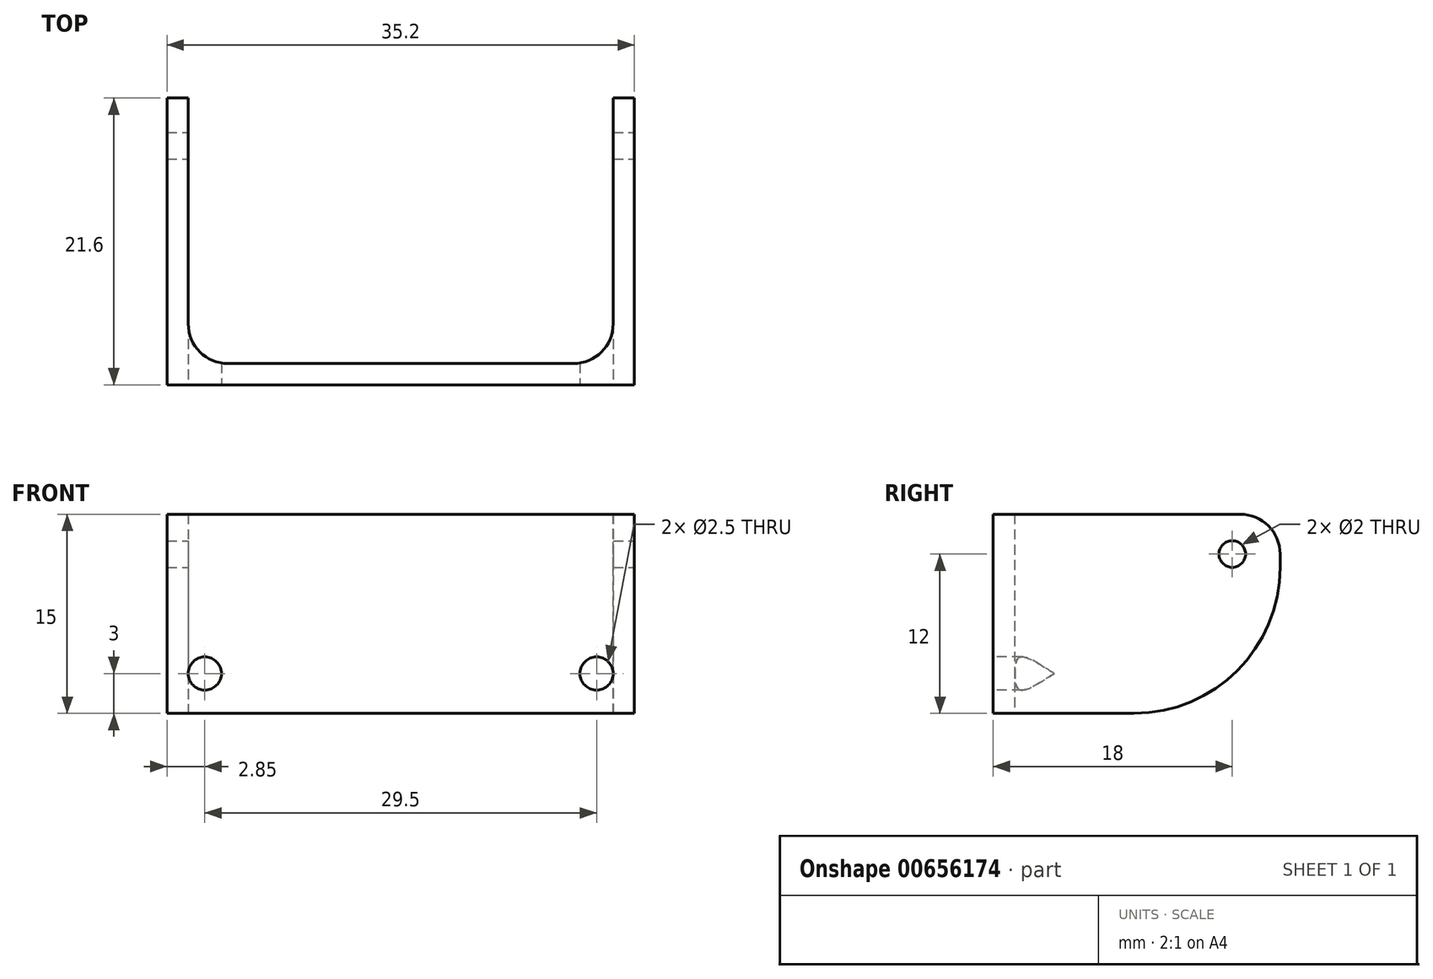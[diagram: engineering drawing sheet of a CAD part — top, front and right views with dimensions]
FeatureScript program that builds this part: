
annotation { "Feature Type Name" : "Feature", "Feature Type Description" : "" }
export const myFeature = defineFeature(function(context is Context, id is Id, definition is map)
    precondition{}
    {
        {
            var Q0;
            Q0=qCreatedBy(makeId("Top.planeOp"),FACE);
            var sketch = newSketch(context, id + "F0", { "sketchPlane" : qUnion([Q0])});
            skLineSegment(sketch, "E0", {"start": v(0, 0) * mm, "end": v(0, -21.6) * mm});
            skLineSegment(sketch, "E1", {"start": v(0, -21.6) * mm, "end": v(35.2, -21.6) * mm});
            skLineSegment(sketch, "E2", {"start": v(35.2, -21.6) * mm, "end": v(35.2, 0) * mm});
            skLineSegment(sketch, "E3", {"start": v(35.2, 0) * mm, "end": v(33.6, 0) * mm});
            skLineSegment(sketch, "E4", {"start": v(33.6, 0) * mm, "end": v(33.6, -17) * mm});
            skLineSegment(sketch, "E5", {"start": v(30.6, -20) * mm, "end": v(4.6, -20) * mm});
            skLineSegment(sketch, "E6", {"start": v(1.6, -17) * mm, "end": v(1.6, 0) * mm});
            skLineSegment(sketch, "E7", {"start": v(1.6, 0) * mm, "end": v(0, 0) * mm});
            skPoint(sketch, "E8.visualSharp", {"position": v(1.6, -20) * mm});
            skArc(sketch, "E8.filletArc", {"start": v(1.6, -17) * mm, "mid": v(2.48, -19.12) * mm, "end": v(4.6, -20) * mm});
            skPoint(sketch, "E9.visualSharp", {"position": v(33.6, -20) * mm});
            skArc(sketch, "E9.filletArc", {"start": v(30.6, -20) * mm, "mid": v(32.72, -19.12) * mm, "end": v(33.6, -17) * mm});
            skSolve(sketch);
        }
        {
            var Q0;
            Q0=makeQuery(id+"F0.imprint","IMPRINT",FACE,{"disambiguationData":[TD([[makeQuery(id+"F0.imprint","IMPRINT",EDGE,{"derivedFrom":sQuery(id+"F0.wireOp",EDGE,"E0")}),1.0]])]});
            extrude(context, id + "F1", {"entities" : qUnion([Q0]), "depth" : 15 * mm});
        }
        {
            var Q0;
            Q0=makeQuery(id+"F1.opExtrude","SWEPT_FACE",FACE,{"disambiguationData":[OSD([sQuery(id+"F0.wireOp",EDGE,"E1")])]});
            var sketch = newSketch(context, id + "F2", { "sketchPlane" : qUnion([Q0])});
            skLineSegment(sketch, "E10", {"start": v(2.85, 3) * mm, "end": v(32.35, 3) * mm, "construction": true});
            skLineSegment(sketch, "E11", {"start": v(17.6, 0) * mm, "end": v(17.6, 3) * mm, "construction": true});
            skCircle(sketch, "E12", {"center": v(2.85, 3) * mm, "radius": 1.25 * mm});
            skCircle(sketch, "E13", {"center": v(32.35, 3) * mm, "radius": 1.25 * mm});
            skSolve(sketch);
        }
        {
            var Q0;
            Q0=qSketchRegion(id+"F2",true);
            extrude(context, id + "F3", {"entities" : qUnion([Q0]), "operationType" : NewBodyOperationType.REMOVE, "oppositeDirection" : true, "depth" : 25 * mm});
        }
        {
            var Q0;
            Q0=makeQuery(id+"F1.opExtrude","SWEPT_FACE",FACE,{"disambiguationData":[OSD([sQuery(id+"F0.wireOp",EDGE,"E2")])]});
            var sketch = newSketch(context, id + "F4", { "sketchPlane" : qUnion([Q0])});
            skCircle(sketch, "E14", {"center": v(-3.6, 12) * mm, "radius": 1 * mm});
            skSolve(sketch);
        }
        {
            var Q0;
            Q0=makeQuery(id+"F4.imprint","IMPRINT",FACE,{"disambiguationData":[TD([[makeQuery(id+"F4.imprint","IMPRINT",EDGE,{"derivedFrom":sQuery(id+"F4.wireOp",EDGE,"E14")}),1.0]])]});
            extrude(context, id + "F5", {"entities" : qUnion([Q0]), "operationType" : NewBodyOperationType.REMOVE, "endBound" : BoundingType.THROUGH_ALL, "oppositeDirection" : true, "depth" : 25 * mm});
        }
        {
            var Q0;
            Q0=makeQuery(id+"F1.opExtrude","CAP_EDGE",EDGE,{"disambiguationData":[OSD([sQuery(id+"F0.wireOp",EDGE,"E7")])],"isStart":false});
            var Q1;
            Q1=makeQuery(id+"F1.opExtrude","CAP_EDGE",EDGE,{"disambiguationData":[OSD([sQuery(id+"F0.wireOp",EDGE,"E3")])],"isStart":false});
            fillet(context, id + "F6", {"entities" : qUnion([Q0, Q1]), "radius" : 3 * mm, "tangentPropagation" : true, "allowEdgeOverflow" : false});
        }
        {
            var Q0;
            Q0=makeQuery(id+"F1.opExtrude","CAP_EDGE",EDGE,{"disambiguationData":[OSD([sQuery(id+"F0.wireOp",EDGE,"E3")])],"isStart":true});
            var Q1;
            Q1=makeQuery(id+"F1.opExtrude","CAP_EDGE",EDGE,{"disambiguationData":[OSD([sQuery(id+"F0.wireOp",EDGE,"E7")])],"isStart":true});
            fillet(context, id + "F7", {"entities" : qUnion([Q0, Q1]), "radius" : 11 * mm, "tangentPropagation" : true, "allowEdgeOverflow" : false});
        }
    });
